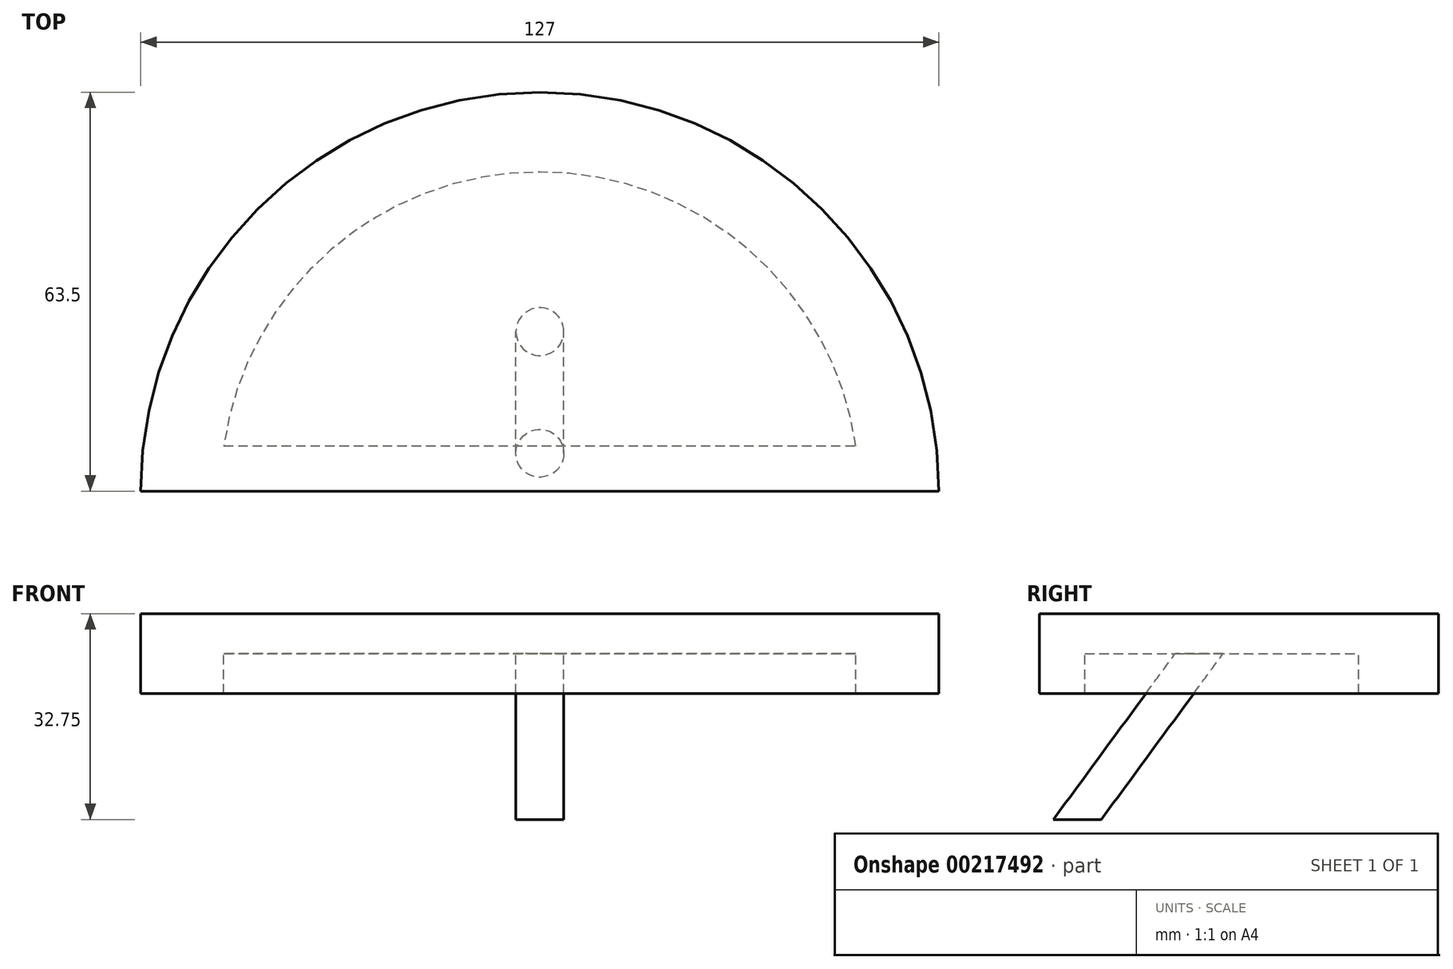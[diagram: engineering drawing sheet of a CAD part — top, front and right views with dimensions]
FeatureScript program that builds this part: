
annotation { "Feature Type Name" : "Feature", "Feature Type Description" : "" }
export const myFeature = defineFeature(function(context is Context, id is Id, definition is map)
    precondition{}
    {
        {
            var Q0;
            Q0=qCreatedBy(makeId("Top.planeOp"),FACE);
            var sketch = newSketch(context, id + "F0", { "sketchPlane" : qUnion([Q0])});
            skArc(sketch, "E0", {"start": v(63.5, 0) * mm, "mid": v(0, 63.5) * mm, "end": v(-63.5, 0) * mm});
            skLineSegment(sketch, "E1", {"start": v(-63.5, 0) * mm, "end": v(63.5, 0) * mm});
            skSolve(sketch);
        }
        {
            var Q0;
            Q0=qSketchRegion(id+"F0",true);
            extrude(context, id + "F1", {"entities" : qUnion([Q0]), "endBound" : BoundingType.SYMMETRIC, "depth" : 12.7 * mm});
        }
        {
            var Q0;
            Q0=qCreatedBy(makeId("Top.planeOp"),FACE);
            var sketch = newSketch(context, id + "F2", { "sketchPlane" : qUnion([Q0])});
            skArc(sketch, "E2", {"start": v(50.28, 7.22) * mm, "mid": v(0, 50.8) * mm, "end": v(-50.28, 7.22) * mm});
            skLineSegment(sketch, "E3", {"start": v(-50.28, 7.22) * mm, "end": v(50.28, 7.22) * mm});
            skSolve(sketch);
        }
        {
            var Q0;
            Q0=qSketchRegion(id+"F2",true);
            extrude(context, id + "F3", {"entities" : qUnion([Q0]), "operationType" : NewBodyOperationType.REMOVE, "oppositeDirection" : true, "depth" : 25.4 * mm});
        }
        {
            var Q0;
            Q0=qCreatedBy(makeId("Top.planeOp"),FACE);
            var sketch = newSketch(context, id + "F4", { "sketchPlane" : qUnion([Q0])});
            skCircle(sketch, "E4", {"center": v(0, 25.4) * mm, "radius": 3.81 * mm});
            skSolve(sketch);
        }
        {
            var Q0;
            Q0=qCreatedBy(makeId("Right.planeOp"),FACE);
            var sketch = newSketch(context, id + "F5", { "sketchPlane" : qUnion([Q0])});
            skLineSegment(sketch, "E5", {"start": v(25.54, 0) * mm, "end": v(6.17, -26.4) * mm});
            skSolve(sketch);
        }
        {
            var Q0;
            Q0=qSketchRegion(id+"F4",true);
            var Q1;
            Q1=qConstructionFilter(qBodyType(qCreatedBy(id+"F5",EDGE),BodyType.WIRE),ConstructionObject.NO);
            sweep(context, id + "F6", {"operationType" : NewBodyOperationType.ADD, "profiles" : qUnion([Q0]), "path" : qUnion([Q1])});
        }
    });
